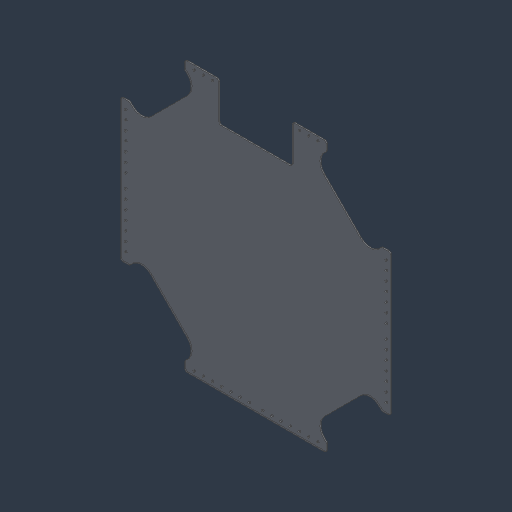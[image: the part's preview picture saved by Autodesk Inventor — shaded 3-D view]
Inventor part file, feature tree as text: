
AUTODESK INVENTOR PART (.ipt)
format: ipt  version: 2024.3 (Build 283343000, 343)  size: 255,488 bytes
history: native  units: mm
features: sketch x3, chamfer x3, pattern_circular x2, other x2, sheet_metal_op x1, extrude x1, hole x1, pattern_linear x1, mirror x1
ambient origin geometry x8: Origin, YZ Plane, XZ Plane, XY Plane, X Axis, Y Axis, Z Axis, Center Point
bodies: Body1 (feature_tree)
feature tree (15):
  sketch  "Sketch5"  dims[d22=749.3mm d23=749.3mm]
  sheet_metal_op  "Face1"
  extrude  "Extrusion3"  Depth=749.3mm
  chamfer  "Corner Round1"
  pattern_circular  "Circular Pattern1"  [2 undecoded]
  chamfer  "Corner Round2"
  hole  "Hole1"  [1 undecoded]
  pattern_linear  "Rectangular Pattern1"  Spacing1=3.175mm  [1 undecoded]
  mirror  "Mirror1"
  pattern_circular  "Circular Pattern2"  [2 undecoded]
  chamfer  "Corner Round3"
  other  "Plate1"
  sketch  "Sketch6"  dims[d24=177.8mm]
  sketch  "Sketch7"  dims[d27=25.4mm d29=36.990947mm d31=158.75mm d32=3.175mm d33=0.0mm d34=0.0mm d35=40.0mm d36=360.0deg d38=6.35mm d39=6.0mm d40=177.8mm d41=12.7mm d42=4.9784mm d43=19.05mm d44=9.779mm d45=6.35mm d46=14.3117mm d47=3.175mm d48=20.594885mm d49=70.0mm d51=25.4mm d52=40.0mm d53=360.0deg d55=107.95mm d56=203.2mm d57=3.175mm d58=0.0mm d59=6.35mm]
  other  "Cut1"
note: 6 required parameter values undecoded (feature->parameter linkage not recoverable at this tier; creation-order binding heuristic only, values carry confidence <= 0.55)
